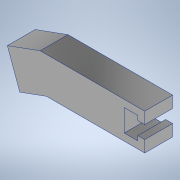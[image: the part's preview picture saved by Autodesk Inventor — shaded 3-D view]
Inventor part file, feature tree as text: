
AUTODESK INVENTOR PART (.ipt)
format: ipt  version: 2022 (Build 260153000, 153)  size: 150,016 bytes
history: native  units: mm
features: extrude x3, sketch x3
ambient origin geometry x8: Origin, YZ Plane, XZ Plane, XY Plane, X Axis, Y Axis, Z Axis, Center Point
bodies: Body1 (feature_tree)
feature tree (6):
  extrude  "Extrusion2"  Depth=5.8mm
  extrude  "Extrusion4"  Depth=12.0mm TaperAngle=0.0deg
  extrude  "Extrusion5"  Depth=15.6mm
  sketch  "Sketch5"  dims[d41=5.8mm d48=44.0mm]
  sketch  "Sketch7"  dims[d50=3.0mm d56=12.0mm d57=0.0mm]
  sketch  "Sketch9"  dims[d63=45.0mm d67=15.6mm d71=0.0mm d72=36.2mm d78=0.0mm d79=0.0mm d80=5.6mm d81=9.5mm d83=15.6mm d84=3.490659mm d85=90.0deg d86=3.490659mm d87=15.0mm d88=0.0mm d89=0.0mm d90=15.0mm]
